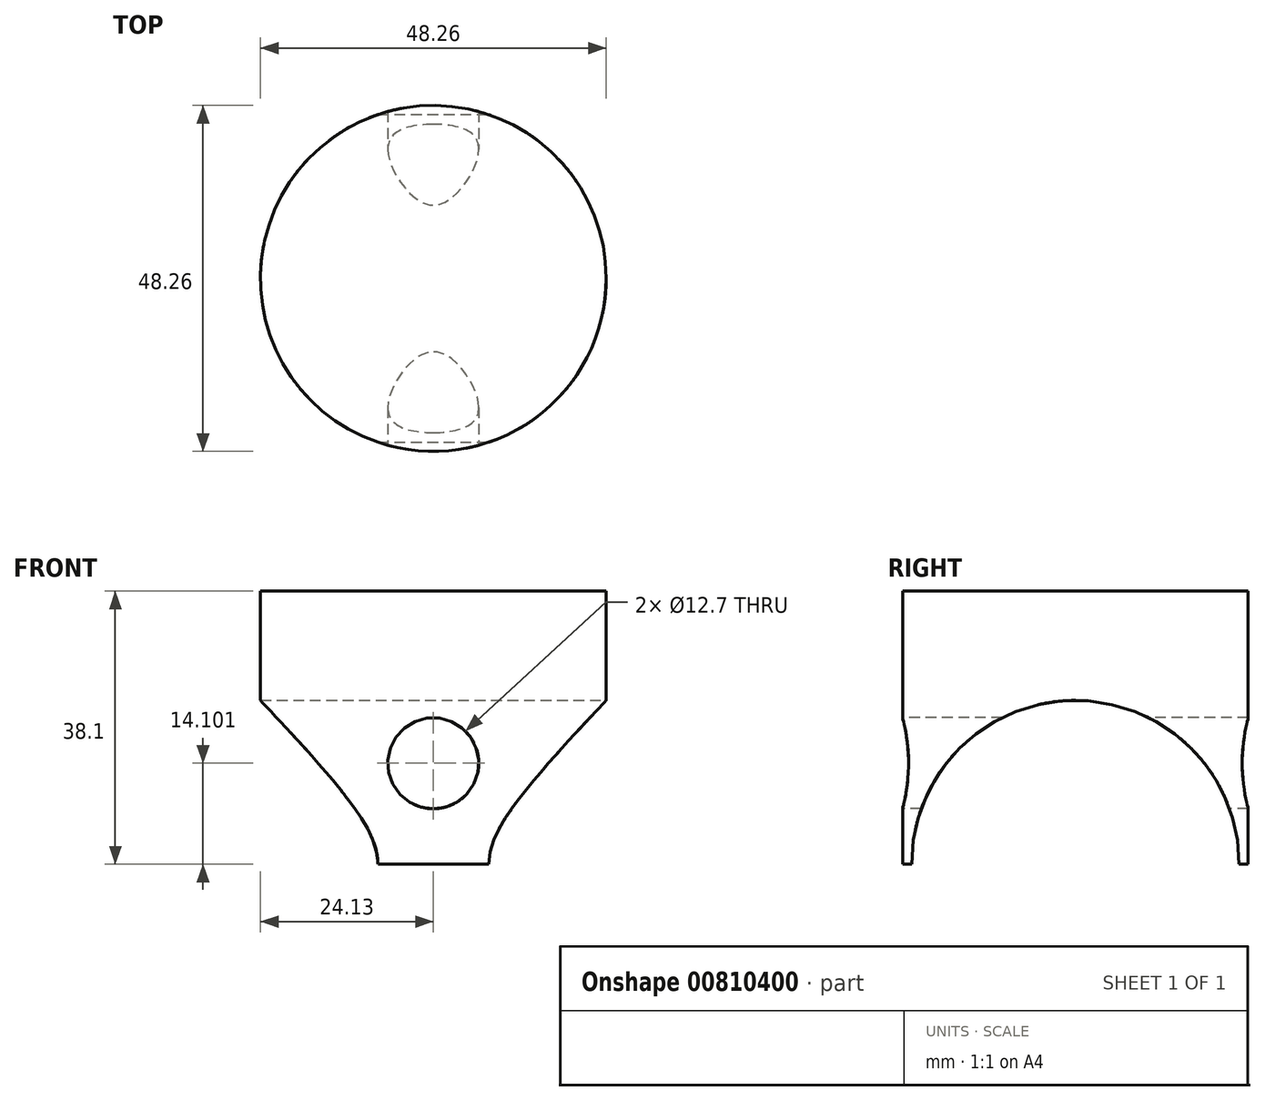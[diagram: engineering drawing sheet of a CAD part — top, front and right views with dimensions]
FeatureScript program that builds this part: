
annotation { "Feature Type Name" : "Feature", "Feature Type Description" : "" }
export const myFeature = defineFeature(function(context is Context, id is Id, definition is map)
    precondition{}
    {
        {
            var Q0;
            Q0=qCreatedBy(makeId("Top.planeOp"),FACE);
            var sketch = newSketch(context, id + "F0", { "sketchPlane" : qUnion([Q0])});
            skCircle(sketch, "E0", {"center": v(0, 0) * mm, "radius": 24.13 * mm});
            skSolve(sketch);
        }
        {
            var Q0;
            Q0=makeQuery(id+"F0.imprint","IMPRINT",FACE,{"disambiguationData":[TD([[makeQuery(id+"F0.imprint","IMPRINT",EDGE,{"derivedFrom":sQuery(id+"F0.wireOp",EDGE,"E0")}),1.0]])]});
            extrude(context, id + "F1", {"entities" : qUnion([Q0]), "depth" : 38.1 * mm, "offsetDistance" : 25.4 * mm});
        }
        {
            var Q0;
            Q0=qCreatedBy(makeId("Right.planeOp"),FACE);
            var sketch = newSketch(context, id + "F2", { "sketchPlane" : qUnion([Q0])});
            skCircle(sketch, "E1", {"center": v(0, 0) * mm, "radius": 22.86 * mm});
            skSolve(sketch);
        }
        {
            var Q0;
            Q0=makeQuery(id+"F2.imprint","IMPRINT",FACE,{"disambiguationData":[TD([[makeQuery(id+"F2.imprint","IMPRINT",EDGE,{"derivedFrom":sQuery(id+"F2.wireOp",EDGE,"E1")}),1.0]])]});
            extrude(context, id + "F3", {"entities" : qUnion([Q0]), "operationType" : NewBodyOperationType.REMOVE, "oppositeDirection" : true, "depth" : 25.4 * mm, "offsetDistance" : 25.4 * mm, "hasSecondDirection" : true, "secondDirectionOppositeDirection" : false, "secondDirectionDepth" : 25.4 * mm});
        }
        {
            var Q0;
            Q0=qCreatedBy(makeId("Front.planeOp"),FACE);
            var sketch = newSketch(context, id + "F4", { "sketchPlane" : qUnion([Q0])});
            skCircle(sketch, "E2", {"center": v(0, 14.1) * mm, "radius": 6.35 * mm});
            skSolve(sketch);
        }
        {
            var Q0;
            Q0=makeQuery(id+"F4.imprint","IMPRINT",FACE,{"disambiguationData":[TD([[makeQuery(id+"F4.imprint","IMPRINT",EDGE,{"derivedFrom":sQuery(id+"F4.wireOp",EDGE,"E2")}),1.0]])]});
            var sketch = newSketch(context, id + "F5", { "sketchPlane" : qUnion([Q0])});
            skSolve(sketch);
        }
        {
            var Q0;
            Q0=makeQuery(id+"F5.imprint","IMPRINT",FACE,{"disambiguationData":[TD([[makeQuery(id+"F5.imprint","IMPRINT",EDGE,{"derivedFrom":makeQuery(id+"F4.imprint","IMPRINT",EDGE,{"derivedFrom":sQuery(id+"F4.wireOp",EDGE,"E2")})}),1.0]])]});
            extrude(context, id + "F6", {"entities" : qUnion([Q0]), "operationType" : NewBodyOperationType.REMOVE, "oppositeDirection" : true, "depth" : 25.4 * mm, "offsetDistance" : 25.4 * mm, "hasSecondDirection" : true, "secondDirectionOppositeDirection" : false, "secondDirectionDepth" : 25.4 * mm});
        }
    });
